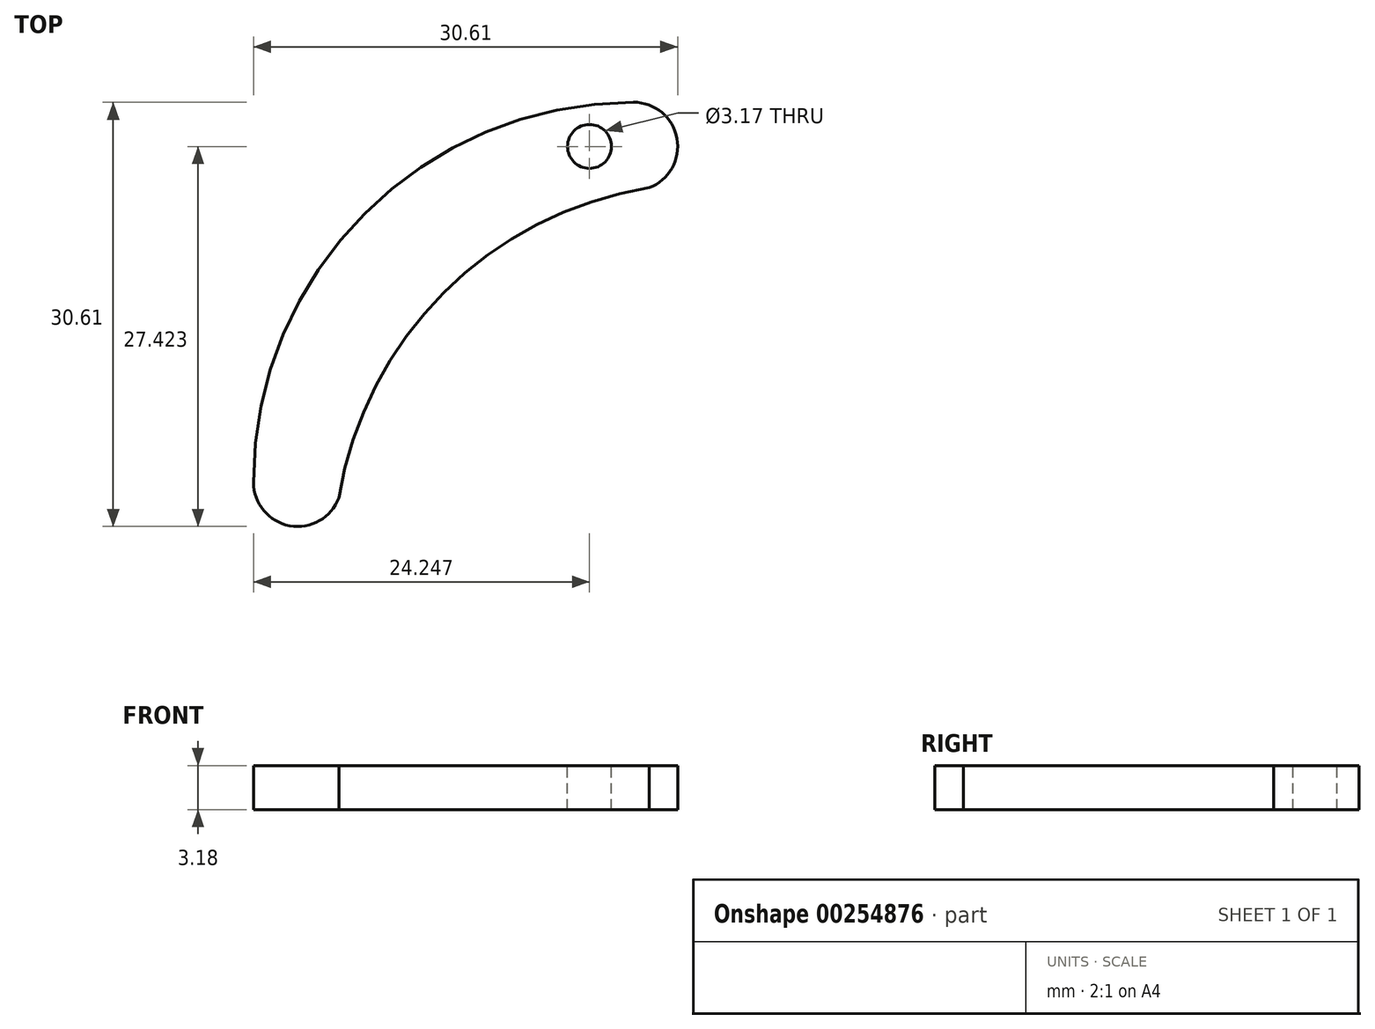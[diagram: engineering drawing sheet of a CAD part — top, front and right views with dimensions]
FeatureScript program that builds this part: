
annotation { "Feature Type Name" : "Feature", "Feature Type Description" : "" }
export const myFeature = defineFeature(function(context is Context, id is Id, definition is map)
    precondition{}
    {
        {
            var Q0;
            Q0=qCreatedBy(makeId("Top.planeOp"),FACE);
            var sketch = newSketch(context, id + "F0", { "sketchPlane" : qUnion([Q0])});
            skArc(sketch, "E0", {"start": v(-4.27, 26.65) * mm, "mid": v(-19.09, 19.09) * mm, "end": v(-26.65, 4.27) * mm});
            skArc(sketch, "E1", {"start": v(-5.4, 32.82) * mm, "mid": v(-24.79, 24.79) * mm, "end": v(-32.82, 5.4) * mm});
            skArc(sketch, "E2", {"start": v(-5.4, 26.45) * mm, "mid": v(-2.21, 29.63) * mm, "end": v(-5.4, 32.82) * mm});
            skPoint(sketch, "E3.orphan", {"position": v(0, 27) * mm});
            skArc(sketch, "E4", {"start": v(-32.82, 5.4) * mm, "mid": v(-29.63, 2.21) * mm, "end": v(-26.45, 5.4) * mm});
            skCircle(sketch, "E5", {"center": v(-8.57, 29.63) * mm, "radius": 1.59 * mm});
            skSolve(sketch);
        }
        {
            var Q0;
            {var subQ0=sQuery(id+"F0.wireOp",EDGE,"E1");Q0=makeQuery(id+"F0.imprint","IMPRINT",FACE,{"disambiguationData":[TD([[makeQuery(id+"F0.imprint","IMPRINT",EDGE,{"derivedFrom":subQ0}),1.0]])]});}
            extrude(context, id + "F1", {"entities" : qUnion([Q0]), "oppositeDirection" : true, "depth" : 3.17 * mm});
        }
    });
